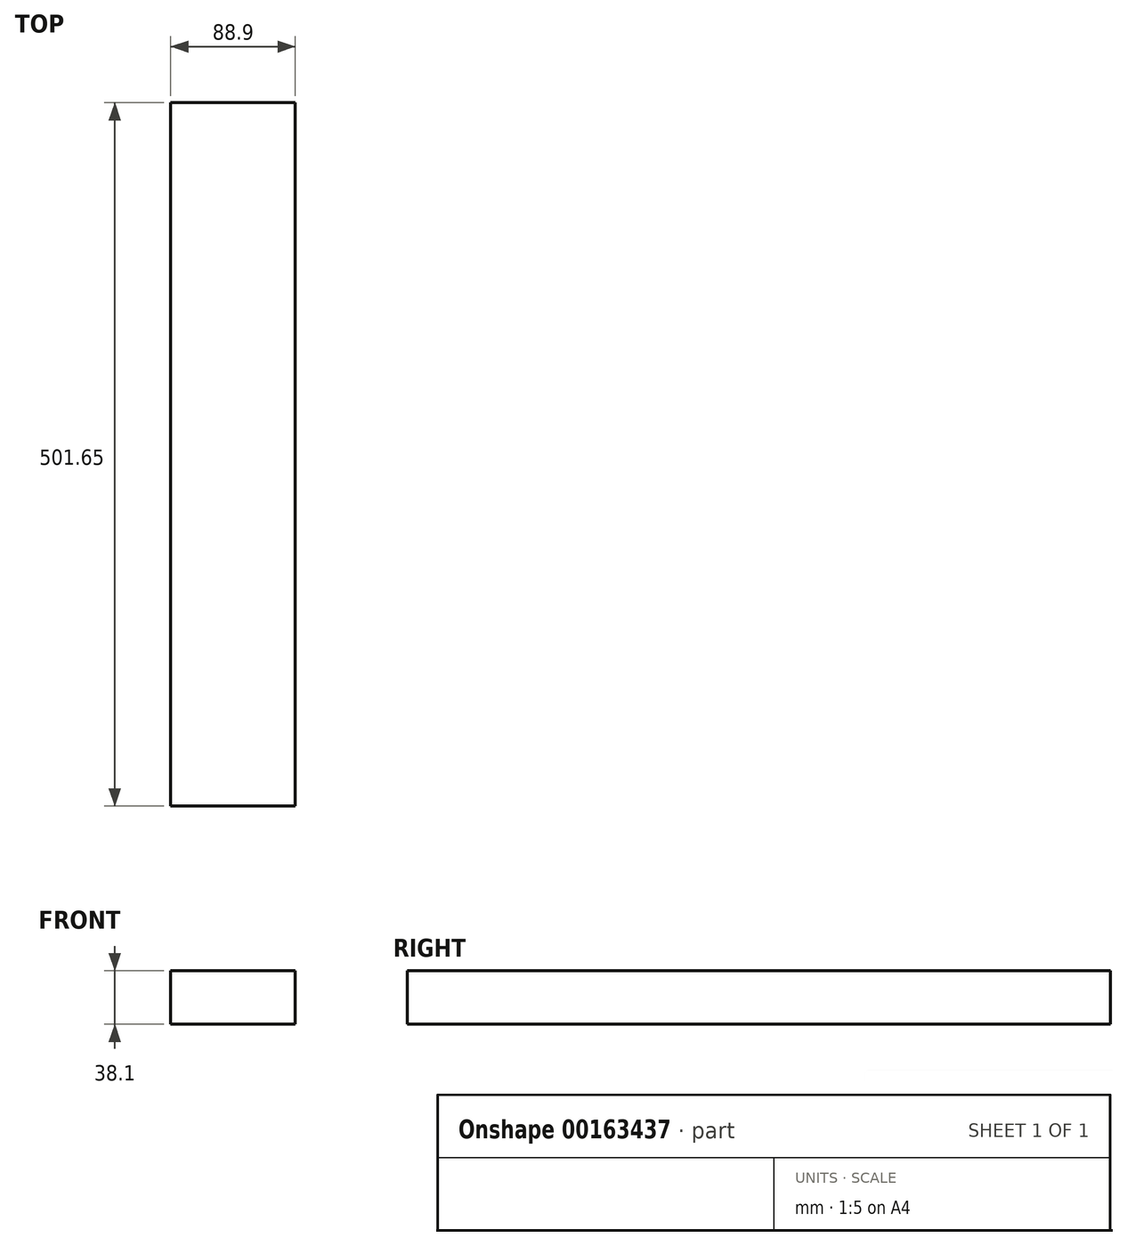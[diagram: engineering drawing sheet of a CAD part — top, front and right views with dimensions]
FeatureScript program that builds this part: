
annotation { "Feature Type Name" : "Feature", "Feature Type Description" : "" }
export const myFeature = defineFeature(function(context is Context, id is Id, definition is map)
    precondition{}
    {
        {
            var Q0;
            Q0=qCreatedBy(makeId("Front.planeOp"),FACE);
            var sketch = newSketch(context, id + "F0", { "sketchPlane" : qUnion([Q0])});
            skLineSegment(sketch, "E0.bottom", {"start": v(0, 0) * mm, "end": v(88.9, 0) * mm});
            skLineSegment(sketch, "E0.top", {"start": v(0, 38.1) * mm, "end": v(88.9, 38.1) * mm});
            skLineSegment(sketch, "E0.left", {"start": v(0, 0) * mm, "end": v(0, 38.1) * mm});
            skLineSegment(sketch, "E0.right", {"start": v(88.9, 0) * mm, "end": v(88.9, 38.1) * mm});
            skSolve(sketch);
        }
        {
            var Q0;
            Q0=makeQuery(id+"F0.imprint","IMPRINT",FACE,{"disambiguationData":[TD([[makeQuery(id+"F0.imprint","IMPRINT",EDGE,{"derivedFrom":sQuery(id+"F0.wireOp",EDGE,"E0.bottom")}),1.0]])]});
            extrude(context, id + "F1", {"entities" : qUnion([Q0]), "depth" : 501.65 * mm});
        }
    });
